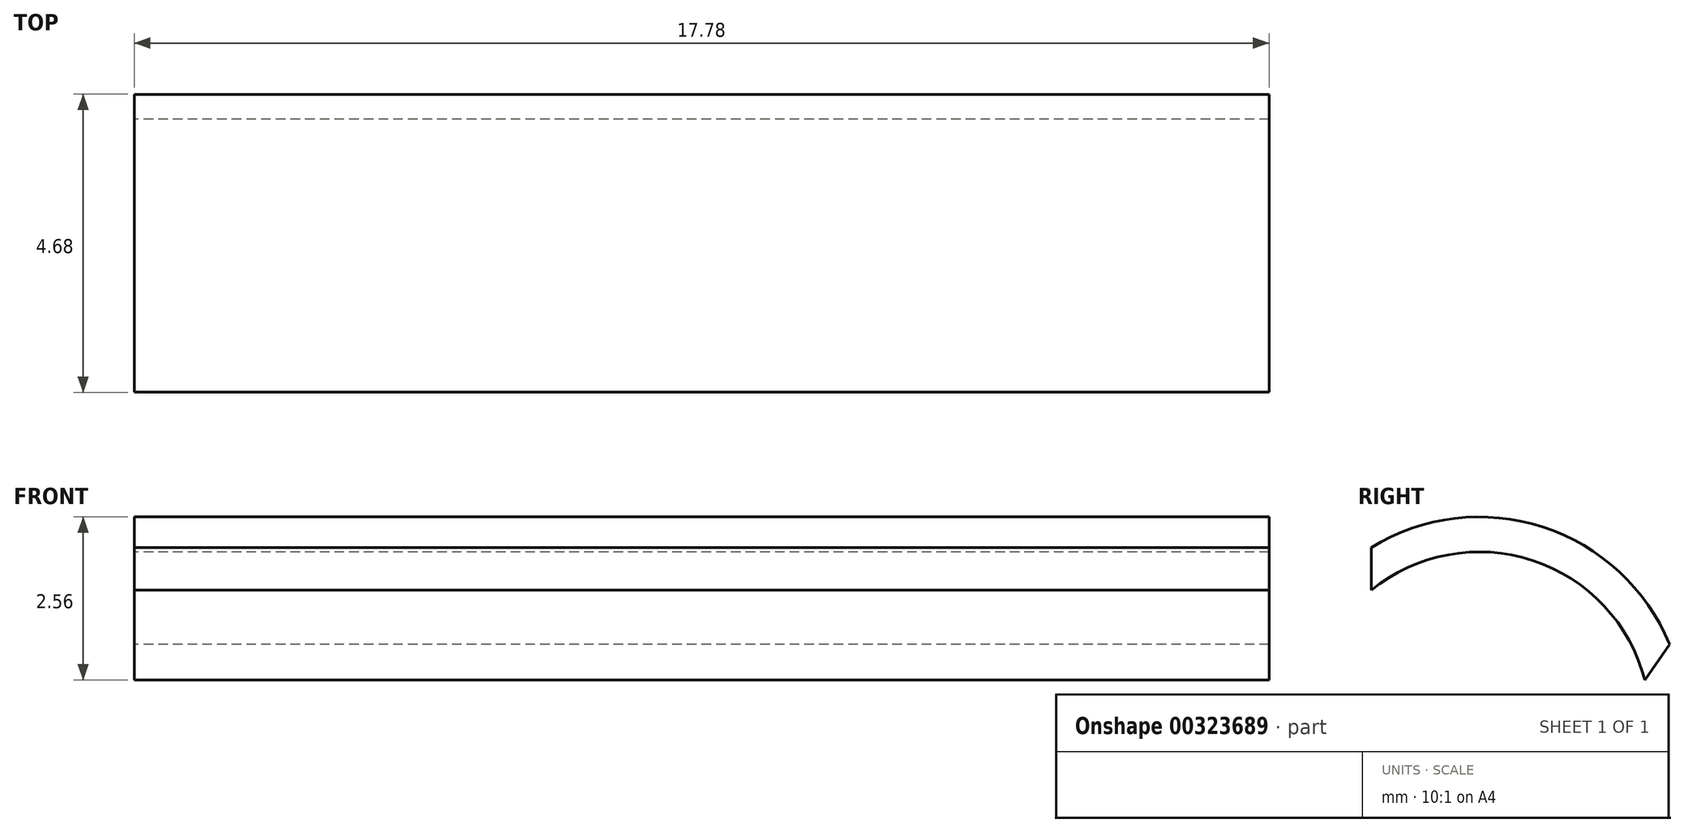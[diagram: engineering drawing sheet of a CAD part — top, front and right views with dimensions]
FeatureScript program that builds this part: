
annotation { "Feature Type Name" : "Feature", "Feature Type Description" : "" }
export const myFeature = defineFeature(function(context is Context, id is Id, definition is map)
    precondition{}
    {
        {
            var Q0;
            Q0=qCreatedBy(makeId("Front.planeOp"),FACE);
            var sketch = newSketch(context, id + "F0", { "sketchPlane" : qUnion([Q0])});
            skLineSegment(sketch, "E0", {"start": v(-25.62, 3.87) * mm, "end": v(-7.84, 3.87) * mm});
            skSolve(sketch);
        }
        {
            var Q0;
            Q0=qCreatedBy(makeId("Right.planeOp"),FACE);
            var sketch = newSketch(context, id + "F1", { "sketchPlane" : qUnion([Q0])});
            skArc(sketch, "E1", {"start": v(1.97, 3.57) * mm, "mid": v(-0.02, 5.4) * mm, "end": v(-2.7, 5.09) * mm});
            skLineSegment(sketch, "E2", {"start": v(1.97, 3.57) * mm, "end": v(1.58, 3) * mm});
            skLineSegment(sketch, "E3", {"start": v(-2.7, 5.09) * mm, "end": v(-2.7, 4.42) * mm});
            skArc(sketch, "E4", {"start": v(1.58, 3) * mm, "mid": v(-0.18, 4.89) * mm, "end": v(-2.7, 4.42) * mm});
            skSolve(sketch);
        }
        {
            var Q0;
            Q0=makeQuery(id+"F1.imprint","IMPRINT",FACE,{"disambiguationData":[TD([[makeQuery(id+"F1.imprint","IMPRINT",EDGE,{"derivedFrom":sQuery(id+"F1.wireOp",EDGE,"rxDMDbI1-PEqe-VxXb-HlIw-UIPhX9hvPTev")}),1.0]])]});
            var Q1;
            Q1=makeQuery(id+"F1.imprint","IMPRINT",FACE,{"disambiguationData":[TD([[makeQuery(id+"F1.imprint","IMPRINT",EDGE,{"derivedFrom":sQuery(id+"F1.wireOp",EDGE,"E1")}),1.0]])]});
            var Q2;
            Q2=sQuery(id+"F0.wireOp",EDGE,"E0");
            sweep(context, id + "F2", {"profiles" : qUnion([Q0, Q1]), "path" : qUnion([Q2])});
        }
    });
